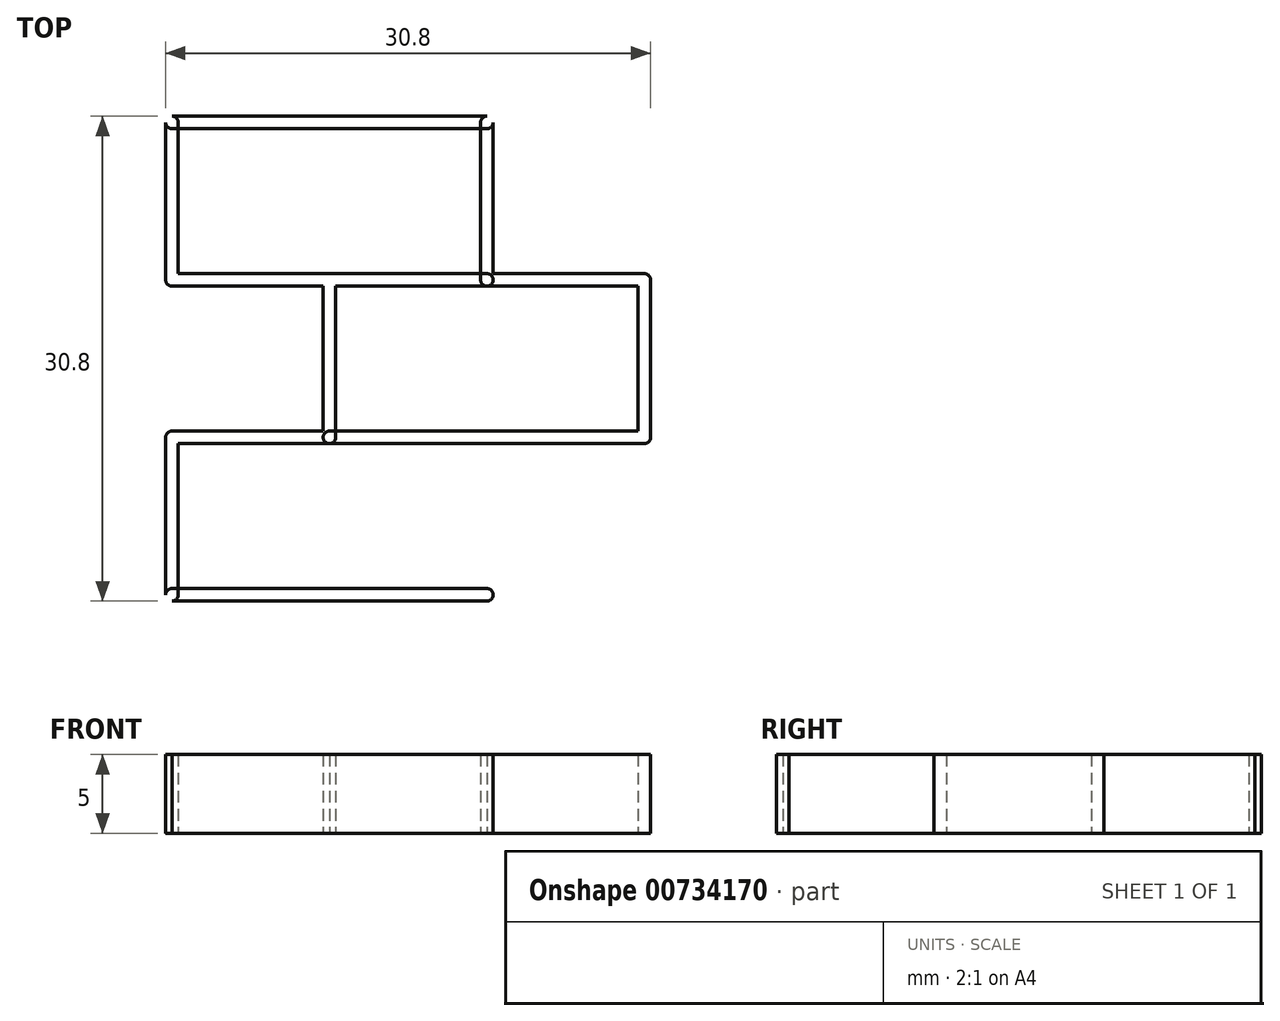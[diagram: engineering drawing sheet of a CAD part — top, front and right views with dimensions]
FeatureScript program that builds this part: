
annotation { "Feature Type Name" : "Feature", "Feature Type Description" : "" }
export const myFeature = defineFeature(function(context is Context, id is Id, definition is map)
    precondition{}
    {
        {
            var Q0;
            Q0=qCreatedBy(makeId("Top.planeOp"),FACE);
            var sketch = newSketch(context, id + "F0", { "sketchPlane" : qUnion([Q0])});
            skLineSegment(sketch, "E0.bottom", {"start": v(-61.89, 49.4) * mm, "end": v(-41.89, 49.4) * mm, "construction": true});
            skLineSegment(sketch, "E0.top", {"start": v(-61.89, 39.4) * mm, "end": v(-41.89, 39.4) * mm, "construction": true});
            skLineSegment(sketch, "E0.left", {"start": v(-61.89, 49.4) * mm, "end": v(-61.89, 39.4) * mm, "construction": true});
            skLineSegment(sketch, "E0.right", {"start": v(-41.89, 49.4) * mm, "end": v(-41.89, 39.4) * mm, "construction": true});
            skLineSegment(sketch, "E1.bottom", {"start": v(-31.89, 29.4) * mm, "end": v(-51.89, 29.4) * mm, "construction": true});
            skLineSegment(sketch, "E1.top", {"start": v(-31.89, 39.4) * mm, "end": v(-51.89, 39.4) * mm, "construction": true});
            skLineSegment(sketch, "E1.left", {"start": v(-31.89, 29.4) * mm, "end": v(-31.89, 39.4) * mm, "construction": true});
            skLineSegment(sketch, "E1.right", {"start": v(-51.89, 29.4) * mm, "end": v(-51.89, 39.4) * mm, "construction": true});
            skLineSegment(sketch, "E2.bottom", {"start": v(-61.89, 19.4) * mm, "end": v(-41.89, 19.4) * mm, "construction": true});
            skLineSegment(sketch, "E2.top", {"start": v(-61.89, 29.4) * mm, "end": v(-41.89, 29.4) * mm, "construction": true});
            skLineSegment(sketch, "E2.left", {"start": v(-61.89, 19.4) * mm, "end": v(-61.89, 29.4) * mm, "construction": true});
            skLineSegment(sketch, "E2.right", {"start": v(-41.89, 19.4) * mm, "end": v(-41.89, 29.4) * mm, "construction": true});
            skArc(sketch, "E3.0.startCap", {"start": v(-61.89, 29) * mm, "mid": v(-62.29, 29.4) * mm, "end": v(-61.89, 29.8) * mm});
            skArc(sketch, "E3.0.endCap", {"start": v(-41.89, 29.8) * mm, "mid": v(-41.49, 29.4) * mm, "end": v(-41.89, 29) * mm});
            skLineSegment(sketch, "E3.0.left", {"start": v(-61.89, 29.8) * mm, "end": v(-41.89, 29.8) * mm});
            skLineSegment(sketch, "E3.0.right", {"start": v(-61.89, 29) * mm, "end": v(-41.89, 29) * mm});
            skArc(sketch, "E3.1.startCap", {"start": v(-61.49, 19.4) * mm, "mid": v(-61.89, 19) * mm, "end": v(-62.29, 19.4) * mm});
            skArc(sketch, "E3.1.endCap", {"start": v(-62.29, 29.4) * mm, "mid": v(-61.89, 29.8) * mm, "end": v(-61.49, 29.4) * mm});
            skLineSegment(sketch, "E3.1.left", {"start": v(-62.29, 19.4) * mm, "end": v(-62.29, 29.4) * mm});
            skLineSegment(sketch, "E3.1.right", {"start": v(-61.49, 19.4) * mm, "end": v(-61.49, 29.4) * mm});
            skArc(sketch, "E3.2.startCap", {"start": v(-31.89, 39.8) * mm, "mid": v(-31.49, 39.4) * mm, "end": v(-31.89, 39) * mm});
            skArc(sketch, "E3.2.endCap", {"start": v(-51.89, 39) * mm, "mid": v(-52.29, 39.4) * mm, "end": v(-51.89, 39.8) * mm});
            skLineSegment(sketch, "E3.2.left", {"start": v(-31.89, 39) * mm, "end": v(-51.89, 39) * mm});
            skLineSegment(sketch, "E3.2.right", {"start": v(-31.89, 39.8) * mm, "end": v(-51.89, 39.8) * mm});
            skArc(sketch, "E3.3.startCap", {"start": v(-61.89, 19) * mm, "mid": v(-62.29, 19.4) * mm, "end": v(-61.89, 19.8) * mm});
            skArc(sketch, "E3.3.endCap", {"start": v(-41.89, 19.8) * mm, "mid": v(-41.49, 19.4) * mm, "end": v(-41.89, 19) * mm});
            skLineSegment(sketch, "E3.3.left", {"start": v(-61.89, 19.8) * mm, "end": v(-41.89, 19.8) * mm});
            skLineSegment(sketch, "E3.3.right", {"start": v(-61.89, 19) * mm, "end": v(-41.89, 19) * mm});
            skArc(sketch, "E3.4.startCap", {"start": v(-31.89, 29.8) * mm, "mid": v(-31.49, 29.4) * mm, "end": v(-31.89, 29) * mm});
            skArc(sketch, "E3.4.endCap", {"start": v(-51.89, 29) * mm, "mid": v(-52.29, 29.4) * mm, "end": v(-51.89, 29.8) * mm});
            skLineSegment(sketch, "E3.4.left", {"start": v(-31.89, 29) * mm, "end": v(-51.89, 29) * mm});
            skLineSegment(sketch, "E3.4.right", {"start": v(-31.89, 29.8) * mm, "end": v(-51.89, 29.8) * mm});
            skArc(sketch, "E3.5.startCap", {"start": v(-61.89, 49) * mm, "mid": v(-62.29, 49.4) * mm, "end": v(-61.89, 49.8) * mm});
            skArc(sketch, "E3.5.endCap", {"start": v(-41.89, 49.8) * mm, "mid": v(-41.49, 49.4) * mm, "end": v(-41.89, 49) * mm});
            skLineSegment(sketch, "E3.5.left", {"start": v(-61.89, 49.8) * mm, "end": v(-41.89, 49.8) * mm});
            skLineSegment(sketch, "E3.5.right", {"start": v(-61.89, 49) * mm, "end": v(-41.89, 49) * mm});
            skArc(sketch, "E3.6.startCap", {"start": v(-41.49, 19.4) * mm, "mid": v(-41.89, 19) * mm, "end": v(-42.29, 19.4) * mm});
            skArc(sketch, "E3.6.endCap", {"start": v(-42.29, 29.4) * mm, "mid": v(-41.89, 29.8) * mm, "end": v(-41.49, 29.4) * mm});
            skLineSegment(sketch, "E3.6.left", {"start": v(-42.29, 19.4) * mm, "end": v(-42.29, 29.4) * mm});
            skLineSegment(sketch, "E3.6.right", {"start": v(-41.49, 19.4) * mm, "end": v(-41.49, 29.4) * mm});
            skArc(sketch, "E3.7.startCap", {"start": v(-61.89, 39) * mm, "mid": v(-62.29, 39.4) * mm, "end": v(-61.89, 39.8) * mm});
            skArc(sketch, "E3.7.endCap", {"start": v(-41.89, 39.8) * mm, "mid": v(-41.49, 39.4) * mm, "end": v(-41.89, 39) * mm});
            skLineSegment(sketch, "E3.7.left", {"start": v(-61.89, 39.8) * mm, "end": v(-41.89, 39.8) * mm});
            skLineSegment(sketch, "E3.7.right", {"start": v(-61.89, 39) * mm, "end": v(-41.89, 39) * mm});
            skArc(sketch, "E3.8.startCap", {"start": v(-31.49, 29.4) * mm, "mid": v(-31.89, 29) * mm, "end": v(-32.29, 29.4) * mm});
            skArc(sketch, "E3.8.endCap", {"start": v(-32.29, 39.4) * mm, "mid": v(-31.89, 39.8) * mm, "end": v(-31.49, 39.4) * mm});
            skLineSegment(sketch, "E3.8.left", {"start": v(-32.29, 29.4) * mm, "end": v(-32.29, 39.4) * mm});
            skLineSegment(sketch, "E3.8.right", {"start": v(-31.49, 29.4) * mm, "end": v(-31.49, 39.4) * mm});
            skArc(sketch, "E3.9.startCap", {"start": v(-51.49, 29.4) * mm, "mid": v(-51.89, 29) * mm, "end": v(-52.29, 29.4) * mm});
            skArc(sketch, "E3.9.endCap", {"start": v(-52.29, 39.4) * mm, "mid": v(-51.89, 39.8) * mm, "end": v(-51.49, 39.4) * mm});
            skLineSegment(sketch, "E3.9.left", {"start": v(-52.29, 29.4) * mm, "end": v(-52.29, 39.4) * mm});
            skLineSegment(sketch, "E3.9.right", {"start": v(-51.49, 29.4) * mm, "end": v(-51.49, 39.4) * mm});
            skArc(sketch, "E3.10.startCap", {"start": v(-62.29, 49.4) * mm, "mid": v(-61.89, 49.8) * mm, "end": v(-61.49, 49.4) * mm});
            skArc(sketch, "E3.10.endCap", {"start": v(-61.49, 39.4) * mm, "mid": v(-61.89, 39) * mm, "end": v(-62.29, 39.4) * mm});
            skLineSegment(sketch, "E3.10.left", {"start": v(-61.49, 49.4) * mm, "end": v(-61.49, 39.4) * mm});
            skLineSegment(sketch, "E3.10.right", {"start": v(-62.29, 49.4) * mm, "end": v(-62.29, 39.4) * mm});
            skArc(sketch, "E3.11.startCap", {"start": v(-42.29, 49.4) * mm, "mid": v(-41.89, 49.8) * mm, "end": v(-41.49, 49.4) * mm});
            skArc(sketch, "E3.11.endCap", {"start": v(-41.49, 39.4) * mm, "mid": v(-41.89, 39) * mm, "end": v(-42.29, 39.4) * mm});
            skLineSegment(sketch, "E3.11.left", {"start": v(-41.49, 49.4) * mm, "end": v(-41.49, 39.4) * mm});
            skLineSegment(sketch, "E3.11.right", {"start": v(-42.29, 49.4) * mm, "end": v(-42.29, 39.4) * mm});
            skSolve(sketch);
        }
        {
            var Q0;
            {var subQ3=sQuery(id+"F0.wireOp",EDGE,"E3.6.right");var subQ5=sQuery(id+"F0.wireOp",EDGE,"E3.3.endCap");var subQ6=makeQuery(id+"F0.imprint","INTERSECT",VERTEX,{"derivedFrom":[subQ5,subQ3]});Q0=makeQuery(id+"F0.imprint","IMPRINT",FACE,{"disambiguationData":[TD([[makeQuery(id+"F0.imprint","IMPRINT",EDGE,{"disambiguationData":[TD([[subQ6,1.0]])],"derivedFrom":subQ5}),1.0]])]});}
            var Q1;
            {var subQ0=sQuery(id+"F0.wireOp",EDGE,"E3.8.endCap");Q1=makeQuery(id+"F0.imprint","IMPRINT",FACE,{"disambiguationData":[TD([[makeQuery(id+"F0.imprint","IMPRINT",EDGE,{"derivedFrom":subQ0}),1.0]])]});}
            var Q2;
            {var subQ6=sQuery(id+"F0.wireOp",EDGE,"E3.0.left");var subQ8=makeQuery(id+"F0.imprint","INTERSECT",VERTEX,{"derivedFrom":[subQ6,sQuery(id+"F0.wireOp",EDGE,"E3.4.endCap")]});Q2=makeQuery(id+"F0.imprint","IMPRINT",FACE,{"disambiguationData":[TD([[makeQuery(id+"F0.imprint","IMPRINT",EDGE,{"disambiguationData":[TD([[subQ8,1.0]])],"derivedFrom":subQ6}),1.0]])]});}
            var Q3;
            {var subQ3=sQuery(id+"F0.wireOp",EDGE,"E3.10.right");Q3=makeQuery(id+"F0.imprint","IMPRINT",FACE,{"disambiguationData":[TD([[makeQuery(id+"F0.imprint","IMPRINT",EDGE,{"derivedFrom":subQ3}),1.0]])]});}
            var Q4;
            Q4=makeQuery(id+"F0.imprint","IMPRINT",FACE,{"disambiguationData":[TD([[makeQuery(id+"F0.imprint","IMPRINT",EDGE,{"derivedFrom":sQuery(id+"F0.wireOp",EDGE,"E3.5.left")}),-1.0]])]});
            var Q5;
            {var subQ5=sQuery(id+"F0.wireOp",EDGE,"E3.1.left");Q5=makeQuery(id+"F0.imprint","IMPRINT",FACE,{"disambiguationData":[TD([[makeQuery(id+"F0.imprint","IMPRINT",EDGE,{"derivedFrom":subQ5}),-1.0]])]});}
            var Q6;
            {var subQ7=sQuery(id+"F0.wireOp",EDGE,"E3.3.right");Q6=makeQuery(id+"F0.imprint","IMPRINT",FACE,{"disambiguationData":[TD([[makeQuery(id+"F0.imprint","IMPRINT",EDGE,{"derivedFrom":subQ7}),1.0]])]});}
            var Q7;
            {var subQ9=sQuery(id+"F0.wireOp",EDGE,"E3.8.right");Q7=makeQuery(id+"F0.imprint","IMPRINT",FACE,{"disambiguationData":[TD([[makeQuery(id+"F0.imprint","IMPRINT",EDGE,{"derivedFrom":subQ9}),1.0]])]});}
            var Q8;
            {var subQ9=sQuery(id+"F0.wireOp",EDGE,"E3.10.endCap");Q8=makeQuery(id+"F0.imprint","IMPRINT",FACE,{"disambiguationData":[TD([[makeQuery(id+"F0.imprint","IMPRINT",EDGE,{"derivedFrom":subQ9}),1.0]])]});}
            var Q9;
            {var subQ0=sQuery(id+"F0.wireOp",EDGE,"E3.11.right");var subQ5=sQuery(id+"F0.wireOp",EDGE,"E3.2.right");var subQ10=makeQuery(id+"F0.imprint","INTERSECT",VERTEX,{"derivedFrom":[subQ5,subQ0]});Q9=makeQuery(id+"F0.imprint","IMPRINT",FACE,{"disambiguationData":[TD([[makeQuery(id+"F0.imprint","IMPRINT",EDGE,{"disambiguationData":[TD([[subQ10,1.0]])],"derivedFrom":subQ5}),-1.0]])]});}
            var Q10;
            {var subQ1=sQuery(id+"F0.wireOp",EDGE,"E3.9.endCap");Q10=makeQuery(id+"F0.imprint","IMPRINT",FACE,{"disambiguationData":[TD([[makeQuery(id+"F0.imprint","IMPRINT",EDGE,{"derivedFrom":subQ1}),1.0]])]});}
            var Q11;
            {var subQ9=sQuery(id+"F0.wireOp",EDGE,"E3.8.startCap");Q11=makeQuery(id+"F0.imprint","IMPRINT",FACE,{"disambiguationData":[TD([[makeQuery(id+"F0.imprint","IMPRINT",EDGE,{"derivedFrom":subQ9}),1.0]])]});}
            var Q12;
            {var subQ3=sQuery(id+"F0.wireOp",EDGE,"E3.1.endCap");Q12=makeQuery(id+"F0.imprint","IMPRINT",FACE,{"disambiguationData":[TD([[makeQuery(id+"F0.imprint","IMPRINT",EDGE,{"derivedFrom":subQ3}),1.0]])]});}
            var Q13;
            {var subQ1=sQuery(id+"F0.wireOp",EDGE,"E3.6.endCap");Q13=makeQuery(id+"F0.imprint","IMPRINT",FACE,{"disambiguationData":[TD([[makeQuery(id+"F0.imprint","IMPRINT",EDGE,{"derivedFrom":subQ1}),1.0]])]});}
            var Q14;
            {var subQ0=sQuery(id+"F0.wireOp",EDGE,"E3.11.endCap");Q14=makeQuery(id+"F0.imprint","IMPRINT",FACE,{"disambiguationData":[TD([[makeQuery(id+"F0.imprint","IMPRINT",EDGE,{"derivedFrom":subQ0}),-1.0]])]});}
            var Q15;
            {var subQ0=sQuery(id+"F0.wireOp",EDGE,"E3.8.endCap");Q15=makeQuery(id+"F0.imprint","IMPRINT",FACE,{"disambiguationData":[TD([[makeQuery(id+"F0.imprint","IMPRINT",EDGE,{"derivedFrom":subQ0}),-1.0]])]});}
            var Q16;
            {var subQ0=sQuery(id+"F0.wireOp",EDGE,"E3.6.startCap");Q16=makeQuery(id+"F0.imprint","IMPRINT",FACE,{"disambiguationData":[TD([[makeQuery(id+"F0.imprint","IMPRINT",EDGE,{"derivedFrom":subQ0}),-1.0]])]});}
            var Q17;
            {var subQ5=sQuery(id+"F0.wireOp",EDGE,"E3.8.startCap");Q17=makeQuery(id+"F0.imprint","IMPRINT",FACE,{"disambiguationData":[TD([[makeQuery(id+"F0.imprint","IMPRINT",EDGE,{"derivedFrom":subQ5}),-1.0]])]});}
            var Q18;
            {var subQ0=sQuery(id+"F0.wireOp",EDGE,"E3.6.endCap");Q18=makeQuery(id+"F0.imprint","IMPRINT",FACE,{"disambiguationData":[TD([[makeQuery(id+"F0.imprint","IMPRINT",EDGE,{"derivedFrom":subQ0}),-1.0]])]});}
            var Q19;
            {var subQ0=sQuery(id+"F0.wireOp",EDGE,"E3.9.endCap");Q19=makeQuery(id+"F0.imprint","IMPRINT",FACE,{"disambiguationData":[TD([[makeQuery(id+"F0.imprint","IMPRINT",EDGE,{"derivedFrom":subQ0}),-1.0]])]});}
            var Q20;
            {var subQ0=sQuery(id+"F0.wireOp",EDGE,"E3.7.endCap");var subQ1=sQuery(id+"F0.wireOp",EDGE,"E3.2.right");var subQ2=makeQuery(id+"F0.imprint","INTERSECT",VERTEX,{"derivedFrom":[subQ1,subQ0]});Q20=makeQuery(id+"F0.imprint","IMPRINT",FACE,{"disambiguationData":[TD([[makeQuery(id+"F0.imprint","IMPRINT",EDGE,{"disambiguationData":[TD([[subQ2,1.0]])],"derivedFrom":subQ1}),1.0]])]});}
            var Q21;
            {var subQ0=sQuery(id+"F0.wireOp",EDGE,"E3.1.endCap");Q21=makeQuery(id+"F0.imprint","IMPRINT",FACE,{"disambiguationData":[TD([[makeQuery(id+"F0.imprint","IMPRINT",EDGE,{"derivedFrom":subQ0}),-1.0]])]});}
            var Q22;
            {var subQ0=sQuery(id+"F0.wireOp",EDGE,"E3.3.startCap");Q22=makeQuery(id+"F0.imprint","IMPRINT",FACE,{"disambiguationData":[TD([[makeQuery(id+"F0.imprint","IMPRINT",EDGE,{"derivedFrom":subQ0}),-1.0]])]});}
            var Q23;
            {var subQ0=sQuery(id+"F0.wireOp",EDGE,"E3.10.startCap");Q23=makeQuery(id+"F0.imprint","IMPRINT",FACE,{"disambiguationData":[TD([[makeQuery(id+"F0.imprint","IMPRINT",EDGE,{"derivedFrom":subQ0}),-1.0]])]});}
            var Q24;
            {var subQ0=sQuery(id+"F0.wireOp",EDGE,"E3.10.endCap");Q24=makeQuery(id+"F0.imprint","IMPRINT",FACE,{"disambiguationData":[TD([[makeQuery(id+"F0.imprint","IMPRINT",EDGE,{"derivedFrom":subQ0}),-1.0]])]});}
            var Q25;
            {var subQ0=sQuery(id+"F0.wireOp",EDGE,"E3.6.right");var subQ1=sQuery(id+"F0.wireOp",EDGE,"E3.0.endCap");var subQ2=makeQuery(id+"F0.imprint","INTERSECT",VERTEX,{"derivedFrom":[subQ1,subQ0]});Q25=makeQuery(id+"F0.imprint","IMPRINT",FACE,{"disambiguationData":[TD([[makeQuery(id+"F0.imprint","IMPRINT",EDGE,{"disambiguationData":[TD([[subQ2,1.0]])],"derivedFrom":subQ0}),1.0]])]});}
            var Q26;
            {var subQ4=sQuery(id+"F0.wireOp",EDGE,"E3.9.startCap");Q26=makeQuery(id+"F0.imprint","IMPRINT",FACE,{"disambiguationData":[TD([[makeQuery(id+"F0.imprint","IMPRINT",EDGE,{"derivedFrom":subQ4}),-1.0]])]});}
            var Q27;
            {var subQ1=sQuery(id+"F0.wireOp",EDGE,"E3.2.endCap");var subQ3=sQuery(id+"F0.wireOp",EDGE,"E3.9.left");var subQ4=makeQuery(id+"F0.imprint","INTERSECT",VERTEX,{"derivedFrom":[subQ1,subQ3]});Q27=makeQuery(id+"F0.imprint","IMPRINT",FACE,{"disambiguationData":[TD([[makeQuery(id+"F0.imprint","IMPRINT",EDGE,{"disambiguationData":[TD([[subQ4,1.0]])],"derivedFrom":subQ3}),-1.0]])]});}
            var Q28;
            {var subQ5=sQuery(id+"F0.wireOp",EDGE,"E3.11.startCap");Q28=makeQuery(id+"F0.imprint","IMPRINT",FACE,{"disambiguationData":[TD([[makeQuery(id+"F0.imprint","IMPRINT",EDGE,{"derivedFrom":subQ5}),-1.0]])]});}
            var Q29;
            {var subQ0=sQuery(id+"F0.wireOp",EDGE,"E3.4.endCap");var subQ1=sQuery(id+"F0.wireOp",EDGE,"E3.0.left");var subQ2=makeQuery(id+"F0.imprint","INTERSECT",VERTEX,{"derivedFrom":[subQ1,subQ0]});Q29=makeQuery(id+"F0.imprint","IMPRINT",FACE,{"disambiguationData":[TD([[makeQuery(id+"F0.imprint","IMPRINT",EDGE,{"disambiguationData":[TD([[subQ2,1.0]])],"derivedFrom":subQ1}),-1.0]])]});}
            extrude(context, id + "F1", {"entities" : qUnion([Q0, Q1, Q2, Q3, Q4, Q5, Q6, Q7, Q8, Q9, Q10, Q11, Q12, Q13, Q14, Q15, Q16, Q17, Q18, Q19, Q20, Q21, Q22, Q23, Q24, Q25, Q26, Q27, Q28, Q29]), "depth" : 5 * mm, "offsetDistance" : 25 * mm});
        }
    });
